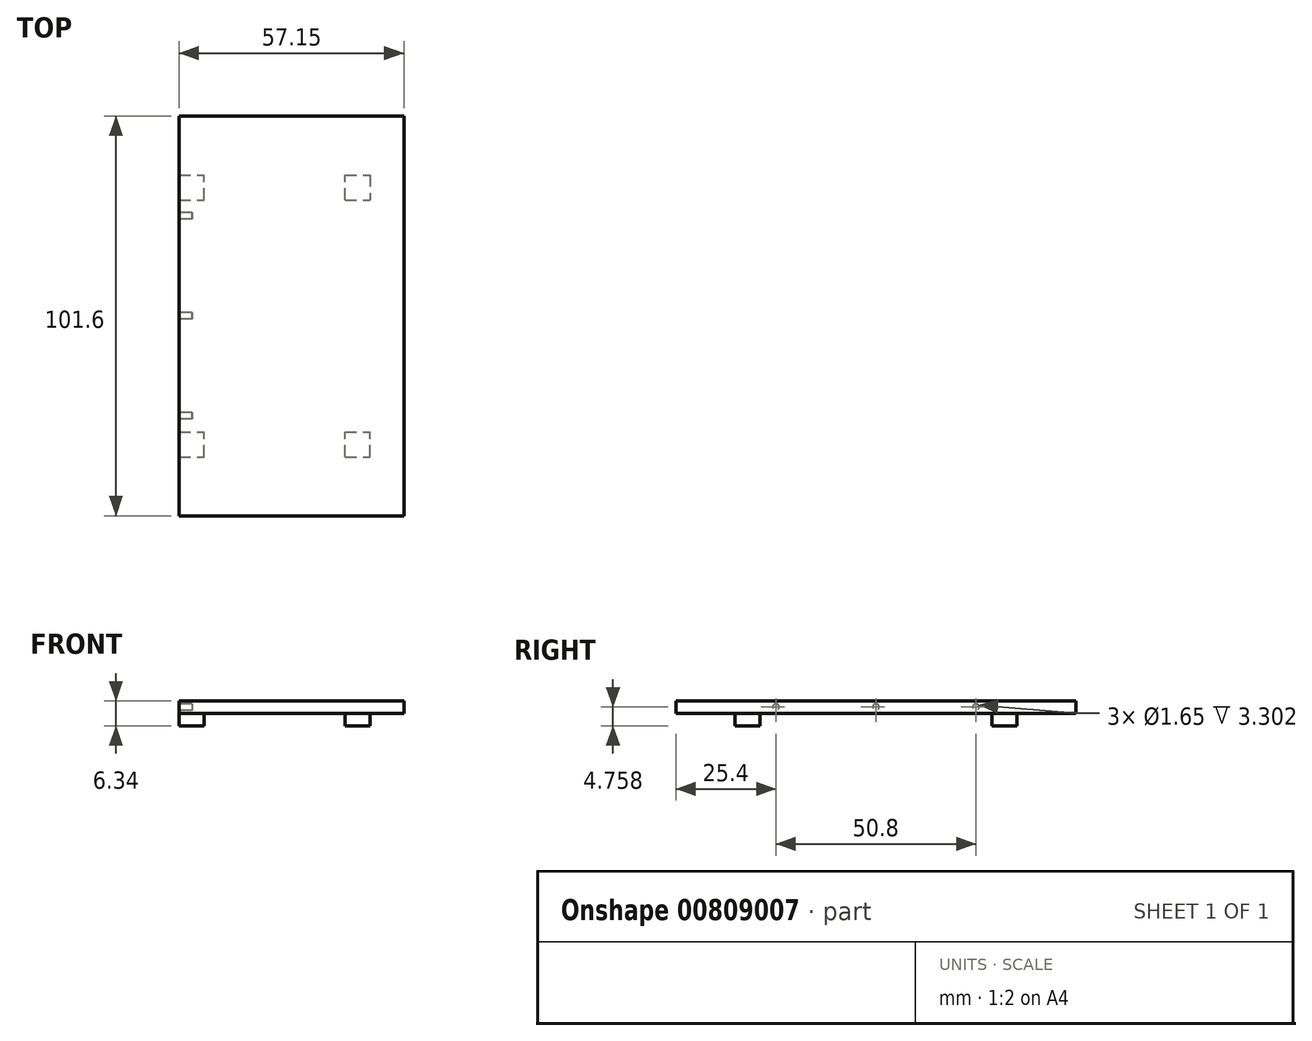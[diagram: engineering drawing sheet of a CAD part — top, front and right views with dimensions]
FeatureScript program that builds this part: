
annotation { "Feature Type Name" : "Feature", "Feature Type Description" : "" }
export const myFeature = defineFeature(function(context is Context, id is Id, definition is map)
    precondition{}
    {
        {
            var Q0;
            Q0=qCreatedBy(makeId("Top.planeOp"),FACE);
            var sketch = newSketch(context, id + "F0", { "sketchPlane" : qUnion([Q0])});
            skLineSegment(sketch, "E0.bottom", {"start": v(-28.57, 50.8) * mm, "end": v(28.58, 50.8) * mm});
            skLineSegment(sketch, "E0.top", {"start": v(-28.58, -50.8) * mm, "end": v(28.57, -50.8) * mm});
            skLineSegment(sketch, "E0.left", {"start": v(-28.57, 50.8) * mm, "end": v(-28.58, -50.8) * mm});
            skLineSegment(sketch, "E0.right", {"start": v(28.58, 50.8) * mm, "end": v(28.57, -50.8) * mm});
            skLineSegment(sketch, "E1", {"start": v(-28.57, 50.8) * mm, "end": v(28.57, -50.8) * mm, "construction": true});
            skLineSegment(sketch, "E2", {"start": v(-28.58, -50.8) * mm, "end": v(28.58, 50.8) * mm, "construction": true});
            skSolve(sketch);
        }
        {
            var Q0;
            Q0=qSketchRegion(id+"F0",true);
            extrude(context, id + "F1", {"entities" : qUnion([Q0]), "depth" : 3.17 * mm, "offsetDistance" : 25.4 * mm});
        }
        {
            var Q0;
            Q0=makeQuery(id+"F1.opExtrude","SWEPT_FACE",FACE,{"disambiguationData":[OSD([sQuery(id+"F0.wireOp",EDGE,"E0.left")])]});
            var sketch = newSketch(context, id + "F2", { "sketchPlane" : qUnion([Q0])});
            skCircle(sketch, "E3", {"center": v(0, 1.59) * mm, "radius": 0.83 * mm});
            skPoint(sketch, "E3.centerSnap0", {"position": v(0, 0) * mm});
            skCircle(sketch, "E4", {"center": v(25.4, 1.59) * mm, "radius": 0.83 * mm});
            skPoint(sketch, "E4.centerSnap0", {"position": v(-50.8, 1.59) * mm});
            skCircle(sketch, "E5", {"center": v(-25.4, 1.59) * mm, "radius": 0.83 * mm});
            skLineSegment(sketch, "E6", {"start": v(0, 0) * mm, "end": v(0, 3.18) * mm, "construction": true});
            skLineSegment(sketch, "E7", {"start": v(-25.4, 1.59) * mm, "end": v(0, 1.59) * mm, "construction": true});
            skLineSegment(sketch, "E8", {"start": v(25.4, 1.59) * mm, "end": v(0, 1.59) * mm, "construction": true});
            skSolve(sketch);
        }
        {
            var Q0;
            Q0 = qSketchRegion(id + "F2", true);
            extrude(context, id + "F3", {"entities" : qUnion([Q0]), "operationType" : NewBodyOperationType.REMOVE, "oppositeDirection" : true, "depth" : 3.3 * mm, "offsetDistance" : 25.4 * mm});
        }
        {
            var Q0;
            Q0=makeQuery(id+"F1.opExtrude","CAP_FACE",FACE,{"disambiguationData":[OSD([sQuery(id+"F0.wireOp",EDGE,"E0.bottom"),sQuery(id+"F0.wireOp",EDGE,"E0.top"),sQuery(id+"F0.wireOp",EDGE,"E0.left"),sQuery(id+"F0.wireOp",EDGE,"E0.right")])],"isStart":true});
            var sketch = newSketch(context, id + "F4", { "sketchPlane" : qUnion([Q0])});
            skLineSegment(sketch, "E9.bottom", {"start": v(-28.58, 35.81) * mm, "end": v(-22.23, 35.81) * mm});
            skLineSegment(sketch, "E9.top", {"start": v(-28.58, 29.46) * mm, "end": v(-22.23, 29.46) * mm});
            skLineSegment(sketch, "E9.left", {"start": v(-28.58, 35.81) * mm, "end": v(-28.58, 29.46) * mm});
            skLineSegment(sketch, "E9.right", {"start": v(-22.23, 35.81) * mm, "end": v(-22.23, 29.46) * mm});
            skLineSegment(sketch, "E10.bottom", {"start": v(-28.58, -29.46) * mm, "end": v(-22.23, -29.46) * mm});
            skLineSegment(sketch, "E10.top", {"start": v(-28.58, -35.81) * mm, "end": v(-22.23, -35.81) * mm});
            skLineSegment(sketch, "E10.left", {"start": v(-28.58, -29.46) * mm, "end": v(-28.58, -35.81) * mm});
            skLineSegment(sketch, "E10.right", {"start": v(-22.23, -29.46) * mm, "end": v(-22.23, -35.81) * mm});
            skLineSegment(sketch, "E11.bottom", {"start": v(13.59, -29.46) * mm, "end": v(19.94, -29.46) * mm});
            skLineSegment(sketch, "E11.top", {"start": v(13.59, -35.81) * mm, "end": v(19.94, -35.81) * mm});
            skLineSegment(sketch, "E11.left", {"start": v(13.59, -29.46) * mm, "end": v(13.59, -35.81) * mm});
            skLineSegment(sketch, "E11.right", {"start": v(19.94, -35.81) * mm, "end": v(19.94, -29.46) * mm});
            skLineSegment(sketch, "E12.bottom", {"start": v(13.59, 35.81) * mm, "end": v(19.94, 35.81) * mm});
            skLineSegment(sketch, "E12.top", {"start": v(13.59, 29.46) * mm, "end": v(19.94, 29.46) * mm});
            skLineSegment(sketch, "E12.left", {"start": v(13.59, 35.81) * mm, "end": v(13.59, 29.46) * mm});
            skLineSegment(sketch, "E12.right", {"start": v(19.94, 35.81) * mm, "end": v(19.94, 29.46) * mm});
            skSolve(sketch);
        }
        {
            var Q0;
            Q0 = qSketchRegion(id + "F4", true);
            extrude(context, id + "F5", {"entities" : qUnion([Q0]), "operationType" : NewBodyOperationType.ADD, "depth" : 3.17 * mm, "offsetDistance" : 25.4 * mm});
        }
    });
